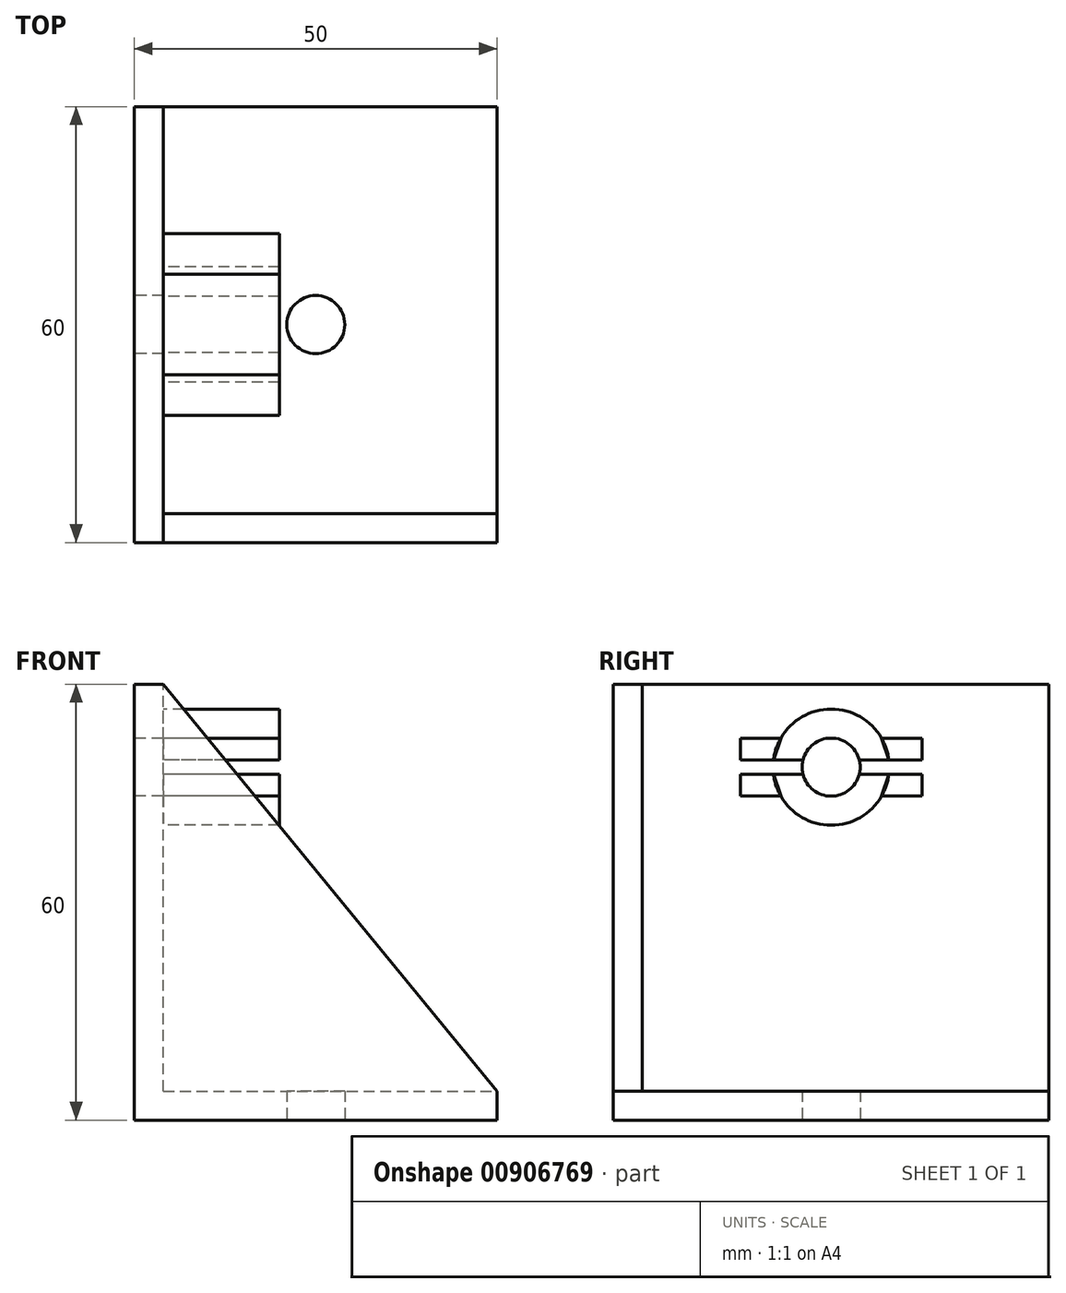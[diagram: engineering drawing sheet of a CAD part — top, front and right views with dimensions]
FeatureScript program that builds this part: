
annotation { "Feature Type Name" : "Feature", "Feature Type Description" : "" }
export const myFeature = defineFeature(function(context is Context, id is Id, definition is map)
    precondition{}
    {
        {
            var Q0;
            Q0=qCreatedBy(makeId("Top.planeOp"),FACE);
            var sketch = newSketch(context, id + "F0", { "sketchPlane" : qUnion([Q0])});
            skLineSegment(sketch, "E0.bottom", {"start": v(25, 30) * mm, "end": v(-25, 30) * mm});
            skLineSegment(sketch, "E0.top", {"start": v(25, -30) * mm, "end": v(-25, -30) * mm});
            skLineSegment(sketch, "E0.left", {"start": v(25, 30) * mm, "end": v(25, -30) * mm});
            skLineSegment(sketch, "E0.right", {"start": v(-25, 30) * mm, "end": v(-25, -30) * mm});
            skPoint(sketch, "E0.middle", {"position": v(0, 0) * mm});
            skCircle(sketch, "E1", {"center": v(0, 0) * mm, "radius": 4 * mm});
            skSolve(sketch);
        }
        {
            var Q0;
            Q0 = qSketchRegion(id + "F0", true);
            extrude(context, id + "F1", {"entities" : qUnion([Q0]), "depth" : 4 * mm, "offsetDistance" : 25 * mm});
        }
        {
            var Q0;
            Q0=makeQuery(id+"F1.opExtrude","SWEPT_FACE",FACE,{"disambiguationData":[OSD([sQuery(id+"F0.wireOp",EDGE,"E0.right")])]});
            var sketch = newSketch(context, id + "F2", { "sketchPlane" : qUnion([Q0])});
            skLineSegment(sketch, "E2.bottom", {"start": v(-30, 0) * mm, "end": v(30, 0) * mm});
            skLineSegment(sketch, "E2.top", {"start": v(-30, 60) * mm, "end": v(30, 60) * mm});
            skLineSegment(sketch, "E2.left", {"start": v(-30, 0) * mm, "end": v(-30, 60) * mm});
            skLineSegment(sketch, "E2.right", {"start": v(30, 0) * mm, "end": v(30, 60) * mm});
            skSolve(sketch);
        }
        {
            var Q0;
            Q0 = qSketchRegion(id + "F2", true);
            extrude(context, id + "F3", {"entities" : qUnion([Q0]), "operationType" : NewBodyOperationType.ADD, "oppositeDirection" : true, "depth" : 4 * mm, "offsetDistance" : 25 * mm});
        }
        {
            var Q0;
            Q0=makeQuery(id+"F3.boolean.opBoolean","MERGE",FACE,{"derivedFrom":[makeQuery(id+"F1.opExtrude","SWEPT_FACE",FACE,{"disambiguationData":[OSD([sQuery(id+"F0.wireOp",EDGE,"E0.top")])]}),makeQuery(id+"F3.opExtrude","SWEPT_FACE",FACE,{"disambiguationData":[OSD([sQuery(id+"F2.wireOp",EDGE,"E2.right")])]})]});
            var sketch = newSketch(context, id + "F4", { "sketchPlane" : qUnion([Q0])});
            skLineSegment(sketch, "E3", {"start": v(-25, 60) * mm, "end": v(-21, 60) * mm});
            skLineSegment(sketch, "E4", {"start": v(-21, 60) * mm, "end": v(25, 4) * mm});
            skLineSegment(sketch, "E5", {"start": v(25, 4) * mm, "end": v(25, 0) * mm});
            skLineSegment(sketch, "E6", {"start": v(25, 0) * mm, "end": v(-25, 0) * mm});
            skLineSegment(sketch, "E7", {"start": v(-25, 0) * mm, "end": v(-25, 60) * mm});
            skSolve(sketch);
        }
        {
            var Q0;
            Q0 = qSketchRegion(id + "F4", true);
            extrude(context, id + "F5", {"entities" : qUnion([Q0]), "operationType" : NewBodyOperationType.ADD, "oppositeDirection" : true, "depth" : 4 * mm, "offsetDistance" : 25 * mm});
        }
        {
            var Q0;
            Q0=makeQuery(id+"F3.boolean.opBoolean","MERGE",FACE,{"derivedFrom":[makeQuery(id+"F1.opExtrude","SWEPT_FACE",FACE,{"disambiguationData":[OSD([sQuery(id+"F0.wireOp",EDGE,"E0.right")])]}),makeQuery(id+"F3.opExtrude","CAP_FACE",FACE,{"disambiguationData":[OSD([sQuery(id+"F2.wireOp",EDGE,"E2.bottom"),sQuery(id+"F2.wireOp",EDGE,"E2.top"),sQuery(id+"F2.wireOp",EDGE,"E2.left"),sQuery(id+"F2.wireOp",EDGE,"E2.right")])],"isStart":true})]});
            var sketch = newSketch(context, id + "F6", { "sketchPlane" : qUnion([Q0])});
            skCircle(sketch, "E8", {"center": v(0, 48.58) * mm, "radius": 4 * mm});
            skCircle(sketch, "E9", {"center": v(0, 48.58) * mm, "radius": 8 * mm});
            skSolve(sketch);
        }
        {
            var Q0;
            Q0=makeQuery(id+"F6.imprint","IMPRINT",FACE,{"disambiguationData":[TD([[makeQuery(id+"F6.imprint","IMPRINT",EDGE,{"derivedFrom":sQuery(id+"F6.wireOp",EDGE,"E8")}),-1.0]])]});
            extrude(context, id + "F7", {"entities" : qUnion([Q0]), "operationType" : NewBodyOperationType.ADD, "oppositeDirection" : true, "depth" : 20 * mm, "offsetDistance" : 25 * mm});
        }
        {
            var Q0;
            Q0=makeQuery(id+"F6.imprint","IMPRINT",FACE,{"disambiguationData":[TD([[makeQuery(id+"F6.imprint","IMPRINT",EDGE,{"derivedFrom":sQuery(id+"F6.wireOp",EDGE,"E8")}),1.0]])]});
            extrude(context, id + "F8", {"entities" : qUnion([Q0]), "operationType" : NewBodyOperationType.REMOVE, "endBound" : BoundingType.THROUGH_ALL, "oppositeDirection" : true, "depth" : 25 * mm, "offsetDistance" : 25 * mm});
        }
        {
            var Q0;
            {var subQ5=sQuery(id+"F2.wireOp",EDGE,"E2.top");Q0=makeQuery(id+"F7.boolean.opBoolean","SPLIT",FACE,{"disambiguationData":[TD([makeQuery(id+"F3.opExtrude","SWEPT_FACE",FACE,{"disambiguationData":[OSD([subQ5])]})])],"derivedFrom":makeQuery(id+"F3.opExtrude","CAP_FACE",FACE,{"disambiguationData":[OSD([sQuery(id+"F2.wireOp",EDGE,"E2.bottom"),subQ5,sQuery(id+"F2.wireOp",EDGE,"E2.left"),sQuery(id+"F2.wireOp",EDGE,"E2.right")])],"isStart":false})});}
            var sketch = newSketch(context, id + "F9", { "sketchPlane" : qUnion([Q0])});
            skLineSegment(sketch, "E10.bottom", {"start": v(12.5, 47.58) * mm, "end": v(-12.5, 47.58) * mm});
            skLineSegment(sketch, "E10.top", {"start": v(12.5, 49.58) * mm, "end": v(-12.5, 49.58) * mm});
            skLineSegment(sketch, "E10.left", {"start": v(12.5, 47.58) * mm, "end": v(12.5, 49.58) * mm});
            skLineSegment(sketch, "E10.right", {"start": v(-12.5, 47.58) * mm, "end": v(-12.5, 49.58) * mm});
            skPoint(sketch, "E10.middle", {"position": v(0, 48.58) * mm});
            skLineSegment(sketch, "E11", {"start": v(-12.5, 49.58) * mm, "end": v(-12.5, 52.58) * mm});
            skLineSegment(sketch, "E12", {"start": v(-12.5, 52.58) * mm, "end": v(-6.93, 52.58) * mm});
            skLineSegment(sketch, "E13", {"start": v(-6.93, 52.58) * mm, "end": v(-7.94, 49.58) * mm});
            skLineSegment(sketch, "E14", {"start": v(-7.94, 49.58) * mm, "end": v(-12.5, 49.58) * mm});
            skLineSegment(sketch, "E15", {"start": v(-12.5, 48.58) * mm, "end": v(12.5, 48.58) * mm, "construction": true});
            skLineSegment(sketch, "E16.MirrorCS", {"start": v(-12.5, 44.58) * mm, "end": v(-6.93, 44.58) * mm});
            skLineSegment(sketch, "E17.MirrorCS", {"start": v(-12.5, 47.58) * mm, "end": v(-12.5, 44.58) * mm});
            skLineSegment(sketch, "E18.MirrorCS", {"start": v(-6.93, 44.58) * mm, "end": v(-7.94, 47.58) * mm});
            skLineSegment(sketch, "E19.MirrorCS", {"start": v(12.5, 52.58) * mm, "end": v(6.93, 52.58) * mm});
            skLineSegment(sketch, "E20.MirrorCS", {"start": v(12.5, 49.58) * mm, "end": v(12.5, 52.58) * mm});
            skLineSegment(sketch, "E21.MirrorCS", {"start": v(6.93, 52.58) * mm, "end": v(7.94, 49.58) * mm});
            skLineSegment(sketch, "E22.MirrorCS", {"start": v(12.5, 44.58) * mm, "end": v(6.93, 44.58) * mm});
            skLineSegment(sketch, "E23.MirrorCS", {"start": v(12.5, 47.58) * mm, "end": v(12.5, 44.58) * mm});
            skLineSegment(sketch, "E24.MirrorCS", {"start": v(6.93, 44.58) * mm, "end": v(7.94, 47.58) * mm});
            skSolve(sketch);
        }
        {
            var Q0;
            Q0 = qSketchRegion(id + "F9", true);
            extrude(context, id + "F10", {"entities" : qUnion([Q0]), "operationType" : NewBodyOperationType.REMOVE, "endBound" : BoundingType.THROUGH_ALL, "depth" : 25 * mm, "offsetDistance" : 25 * mm});
        }
        {
            var Q0;
            Q0=makeQuery(id+"F9.imprint","IMPRINT",FACE,{"disambiguationData":[TD([[makeQuery(id+"F9.imprint","IMPRINT",EDGE,{"derivedFrom":sQuery(id+"F9.wireOp",EDGE,"E11")}),-1.0]])]});
            var Q1;
            {var subQ5=sQuery(id+"F9.wireOp",EDGE,"E16.MirrorCS");Q1=makeQuery(id+"F9.imprint","IMPRINT",FACE,{"disambiguationData":[TD([[makeQuery(id+"F9.imprint","IMPRINT",EDGE,{"derivedFrom":subQ5}),1.0]])]});}
            var Q2;
            {var subQ5=sQuery(id+"F9.wireOp",EDGE,"E19.MirrorCS");Q2=makeQuery(id+"F9.imprint","IMPRINT",FACE,{"disambiguationData":[TD([[makeQuery(id+"F9.imprint","IMPRINT",EDGE,{"derivedFrom":subQ5}),1.0]])]});}
            var Q3;
            {var subQ5=sQuery(id+"F9.wireOp",EDGE,"E22.MirrorCS");Q3=makeQuery(id+"F9.imprint","IMPRINT",FACE,{"disambiguationData":[TD([[makeQuery(id+"F9.imprint","IMPRINT",EDGE,{"derivedFrom":subQ5}),-1.0]])]});}
            extrude(context, id + "F11", {"entities" : qUnion([Q0, Q1, Q2, Q3]), "depth" : 16 * mm, "offsetDistance" : 25 * mm});
        }
    });
